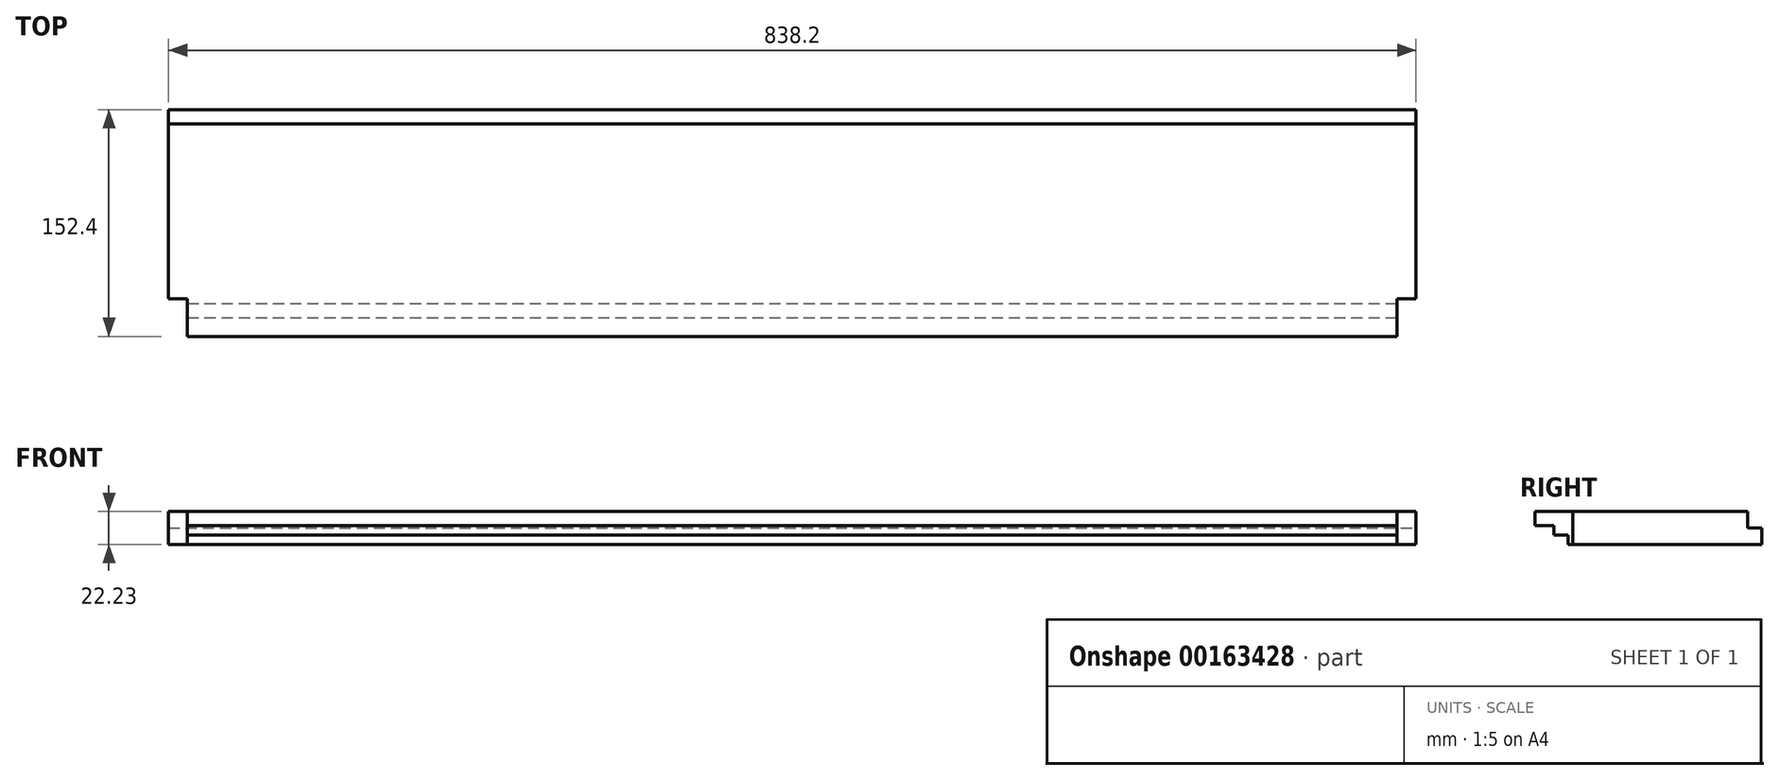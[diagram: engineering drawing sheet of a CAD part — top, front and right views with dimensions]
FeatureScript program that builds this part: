
annotation { "Feature Type Name" : "Feature", "Feature Type Description" : "" }
export const myFeature = defineFeature(function(context is Context, id is Id, definition is map)
    precondition{}
    {
        {
            var Q0;
            Q0=qCreatedBy(makeId("Top.planeOp"),FACE);
            var sketch = newSketch(context, id + "F0", { "sketchPlane" : qUnion([Q0])});
            skLineSegment(sketch, "E0.bottom", {"start": v(0, 0) * mm, "end": v(419.1, 0) * mm});
            skLineSegment(sketch, "E0.top", {"start": v(0, 152.4) * mm, "end": v(419.1, 152.4) * mm});
            skLineSegment(sketch, "E0.left", {"start": v(0, 0) * mm, "end": v(0, 152.4) * mm});
            skLineSegment(sketch, "E0.right", {"start": v(419.1, 0) * mm, "end": v(419.1, 152.4) * mm});
            skSolve(sketch);
        }
        {
            var Q0;
            Q0=makeQuery(id+"F0.imprint","IMPRINT",FACE,{"disambiguationData":[TD([[makeQuery(id+"F0.imprint","IMPRINT",EDGE,{"derivedFrom":sQuery(id+"F0.wireOp",EDGE,"E0.bottom")}),1.0]])]});
            extrude(context, id + "F1", {"entities" : qUnion([Q0]), "depth" : 22.22 * mm});
        }
        {
            var Q0;
            Q0=makeQuery(id+"F1.opExtrude","CAP_FACE",FACE,{"disambiguationData":[OSD([sQuery(id+"F0.wireOp",EDGE,"E0.bottom"),sQuery(id+"F0.wireOp",EDGE,"E0.top"),sQuery(id+"F0.wireOp",EDGE,"E0.left"),sQuery(id+"F0.wireOp",EDGE,"E0.right")])],"isStart":false});
            var sketch = newSketch(context, id + "F2", { "sketchPlane" : qUnion([Q0])});
            skLineSegment(sketch, "E1.bottom", {"start": v(0, 0) * mm, "end": v(12.7, 0) * mm});
            skLineSegment(sketch, "E1.top", {"start": v(0, 25.4) * mm, "end": v(12.7, 25.4) * mm});
            skLineSegment(sketch, "E1.left", {"start": v(0, 0) * mm, "end": v(0, 25.4) * mm});
            skLineSegment(sketch, "E1.right", {"start": v(12.7, 0) * mm, "end": v(12.7, 25.4) * mm});
            skSolve(sketch);
        }
        {
            var Q0;
            Q0=makeQuery(id+"F2.imprint","IMPRINT",FACE,{"disambiguationData":[TD([[makeQuery(id+"F2.imprint","IMPRINT",EDGE,{"derivedFrom":sQuery(id+"F2.wireOp",EDGE,"E1.bottom")}),1.0]])]});
            extrude(context, id + "F3", {"entities" : qUnion([Q0]), "operationType" : NewBodyOperationType.REMOVE, "endBound" : BoundingType.THROUGH_ALL, "oppositeDirection" : true, "depth" : 25.4 * mm});
        }
        {
            var Q0;
            Q0=makeQuery(id+"F1.opExtrude","SWEPT_FACE",FACE,{"disambiguationData":[OSD([sQuery(id+"F0.wireOp",EDGE,"E0.right")])]});
            var sketch = newSketch(context, id + "F4", { "sketchPlane" : qUnion([Q0])});
            skLineSegment(sketch, "E2.bottom", {"start": v(152.4, 22.23) * mm, "end": v(142.87, 22.23) * mm});
            skLineSegment(sketch, "E2.top", {"start": v(152.4, 11.11) * mm, "end": v(142.87, 11.11) * mm});
            skLineSegment(sketch, "E2.left", {"start": v(152.4, 22.23) * mm, "end": v(152.4, 11.11) * mm});
            skLineSegment(sketch, "E2.right", {"start": v(142.87, 22.23) * mm, "end": v(142.87, 11.11) * mm});
            skLineSegment(sketch, "E3", {"start": v(0, 0) * mm, "end": v(0, 12.7) * mm});
            skLineSegment(sketch, "E4", {"start": v(0, 12.7) * mm, "end": v(12.7, 12.7) * mm});
            skLineSegment(sketch, "E5", {"start": v(12.7, 12.7) * mm, "end": v(12.7, 6.35) * mm});
            skLineSegment(sketch, "E6", {"start": v(12.7, 6.35) * mm, "end": v(22.22, 6.35) * mm});
            skLineSegment(sketch, "E7", {"start": v(22.22, 6.35) * mm, "end": v(22.22, 0) * mm});
            skLineSegment(sketch, "E8", {"start": v(22.22, 0) * mm, "end": v(0, 0) * mm});
            skSolve(sketch);
        }
        {
            var Q0;
            Q0=makeQuery(id+"F4.imprint","IMPRINT",FACE,{"disambiguationData":[TD([[makeQuery(id+"F4.imprint","IMPRINT",EDGE,{"derivedFrom":sQuery(id+"F4.wireOp",EDGE,"E3")}),1.0]])]});
            var Q1;
            Q1=makeQuery(id+"F4.imprint","IMPRINT",FACE,{"disambiguationData":[TD([[makeQuery(id+"F4.imprint","IMPRINT",EDGE,{"derivedFrom":sQuery(id+"F4.wireOp",EDGE,"E2.bottom")}),-1.0]])]});
            extrude(context, id + "F5", {"entities" : qUnion([Q0, Q1]), "operationType" : NewBodyOperationType.REMOVE, "endBound" : BoundingType.THROUGH_ALL, "oppositeDirection" : true, "depth" : 25.4 * mm});
        }
        {
            var Q0;
            Q0=makeQuery(id+"F1.opExtrude","SWEPT_BODY",BODY,{"disambiguationData":[OSD([sQuery(id+"F0.wireOp",EDGE,"E0.bottom"),sQuery(id+"F0.wireOp",EDGE,"E0.top"),sQuery(id+"F0.wireOp",EDGE,"E0.left"),sQuery(id+"F0.wireOp",EDGE,"E0.right")])]});
            var Q1;
            Q1=makeQuery(id+"F1.opExtrude","SWEPT_FACE",FACE,{"disambiguationData":[OSD([sQuery(id+"F0.wireOp",EDGE,"E0.right")])]});
            mirror(context, id + "F6", {"operationType" : NewBodyOperationType.ADD, "entities" : qUnion([Q0]), "mirrorPlane" : qUnion([Q1])});
        }
    });
